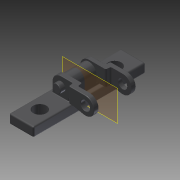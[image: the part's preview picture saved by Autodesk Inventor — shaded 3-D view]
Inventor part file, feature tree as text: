
AUTODESK INVENTOR PART (.ipt)
format: ipt  version: 2015 (Build 190159000, 159)  size: 584,192 bytes
history: native  units: in
note: dims shown in document units (in); Inventor stores cm internally (conversion verified against a paired STEP export)
features: other x4, plane x1, imported_body x1
ambient origin geometry x8: Origin, YZ Plane, XZ Plane, XY Plane, X Axis, Y Axis, Z Axis, Center Point
bodies: Solid1 (feature_tree)
feature tree (6):
  other  "Chain HS Mount"
  other  "mid plane"
  plane  "Work Plane2"
  imported_body  "Base1"
  other  "Work Axis3"
  other  "Work Axis4"
